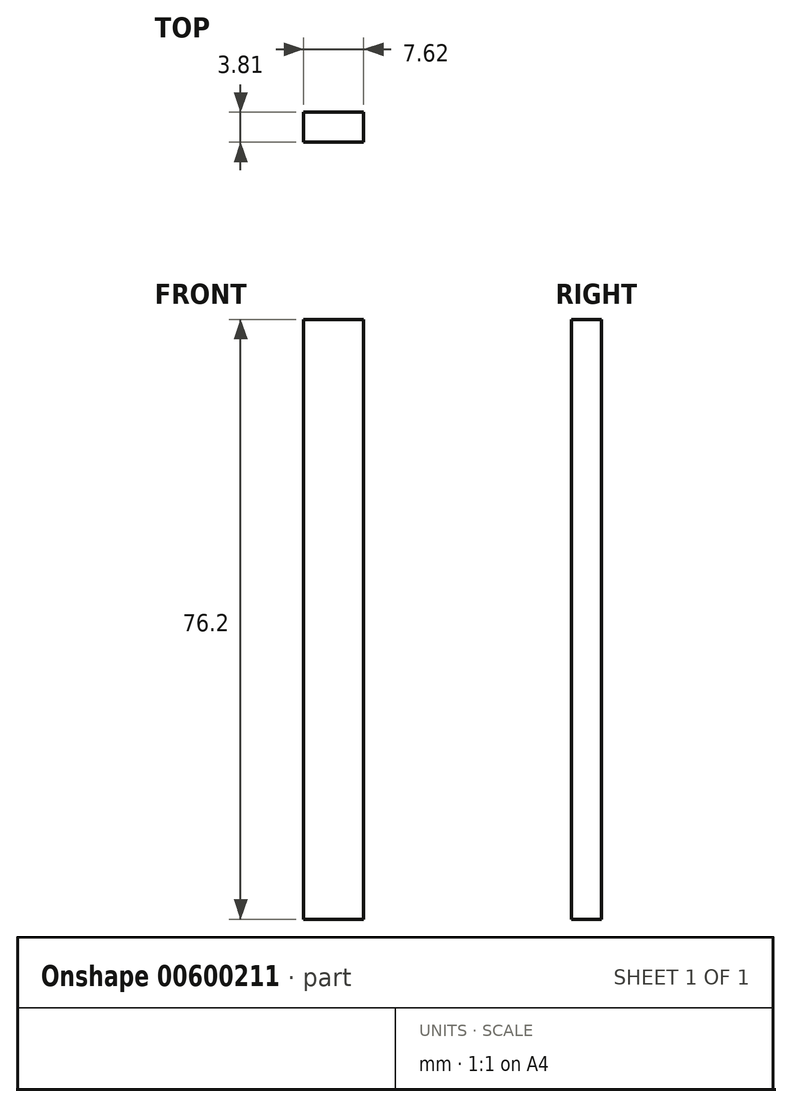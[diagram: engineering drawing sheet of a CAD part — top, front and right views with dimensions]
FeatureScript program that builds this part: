
annotation { "Feature Type Name" : "Feature", "Feature Type Description" : "" }
export const myFeature = defineFeature(function(context is Context, id is Id, definition is map)
    precondition{}
    {
        {
            var Q0;
            Q0=qCreatedBy(makeId("Top.planeOp"),FACE);
            var sketch = newSketch(context, id + "F0", { "sketchPlane" : qUnion([Q0])});
            skLineSegment(sketch, "E0.bottom", {"start": v(0, 0) * mm, "end": v(7.62, 0) * mm});
            skLineSegment(sketch, "E0.top", {"start": v(0, 3.81) * mm, "end": v(7.62, 3.81) * mm});
            skLineSegment(sketch, "E0.left", {"start": v(0, 0) * mm, "end": v(0, 3.8) * mm});
            skLineSegment(sketch, "E0.right", {"start": v(7.62, 0) * mm, "end": v(7.62, 3.81) * mm});
            skSolve(sketch);
        }
        {
            var Q0;
            Q0=makeQuery(id+"F0.imprint","IMPRINT",FACE,{"disambiguationData":[TD([[makeQuery(id+"F0.imprint","IMPRINT",EDGE,{"derivedFrom":sQuery(id+"F0.wireOp",EDGE,"E0.bottom")}),1.0]])]});
            extrude(context, id + "F1", {"entities" : qUnion([Q0]), "depth" : 76.2 * mm, "offsetDistance" : 25.4 * mm});
        }
    });
